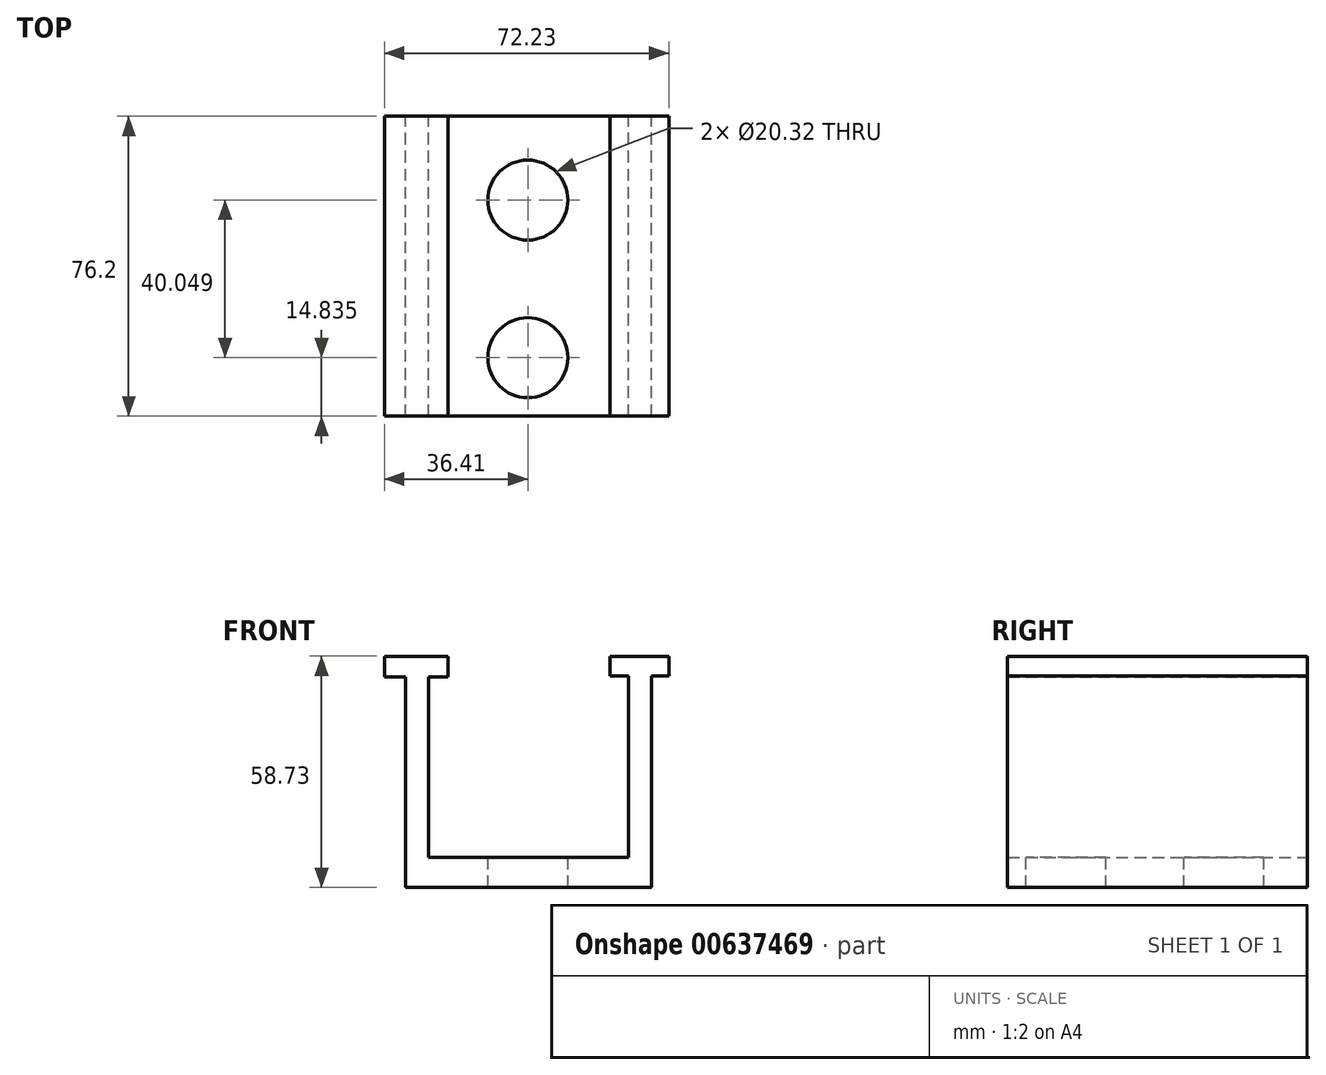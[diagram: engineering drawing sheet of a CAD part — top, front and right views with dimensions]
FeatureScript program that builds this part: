
annotation { "Feature Type Name" : "Feature", "Feature Type Description" : "" }
export const myFeature = defineFeature(function(context is Context, id is Id, definition is map)
    precondition{}
    {
        {
            var Q0;
            Q0=qCreatedBy(makeId("Front.planeOp"),FACE);
            var sketch = newSketch(context, id + "F0", { "sketchPlane" : qUnion([Q0])});
            skLineSegment(sketch, "E0.bottom", {"start": v(-53.88, 30.54) * mm, "end": v(-37.73, 30.54) * mm});
            skLineSegment(sketch, "E0.top", {"start": v(-53.88, 25.25) * mm, "end": v(-37.73, 25.25) * mm});
            skLineSegment(sketch, "E0.left", {"start": v(-53.88, 30.54) * mm, "end": v(-53.88, 25.25) * mm});
            skLineSegment(sketch, "E0.right", {"start": v(-37.73, 30.54) * mm, "end": v(-37.73, 25.25) * mm});
            skLineSegment(sketch, "E1.bottom", {"start": v(3.38, 30.54) * mm, "end": v(18.35, 30.54) * mm});
            skLineSegment(sketch, "E1.top", {"start": v(3.38, 25.54) * mm, "end": v(18.35, 25.54) * mm});
            skLineSegment(sketch, "E1.left", {"start": v(3.38, 30.54) * mm, "end": v(3.38, 25.54) * mm});
            skLineSegment(sketch, "E1.right", {"start": v(18.35, 30.54) * mm, "end": v(18.35, 25.54) * mm});
            skLineSegment(sketch, "E2.bottom", {"start": v(-48.6, 25.25) * mm, "end": v(-42.72, 25.25) * mm});
            skLineSegment(sketch, "E2.top", {"start": v(-48.6, -20.55) * mm, "end": v(-42.72, -20.55) * mm});
            skLineSegment(sketch, "E2.left", {"start": v(-48.6, 25.25) * mm, "end": v(-48.6, -20.55) * mm});
            skLineSegment(sketch, "E2.right", {"start": v(-42.72, 25.25) * mm, "end": v(-42.72, -20.55) * mm});
            skLineSegment(sketch, "E3.bottom", {"start": v(8.07, 25.54) * mm, "end": v(13.95, 25.54) * mm});
            skLineSegment(sketch, "E3.top", {"start": v(8.07, -20.55) * mm, "end": v(13.95, -20.55) * mm});
            skLineSegment(sketch, "E3.left", {"start": v(8.07, 25.54) * mm, "end": v(8.07, -20.55) * mm});
            skLineSegment(sketch, "E3.right", {"start": v(13.95, 25.54) * mm, "end": v(13.95, -20.55) * mm});
            skLineSegment(sketch, "E4.bottom", {"start": v(-48.6, -20.55) * mm, "end": v(13.95, -20.55) * mm});
            skLineSegment(sketch, "E4.top", {"start": v(-48.6, -28.19) * mm, "end": v(13.95, -28.19) * mm});
            skLineSegment(sketch, "E4.left", {"start": v(-48.6, -20.55) * mm, "end": v(-48.6, -28.19) * mm});
            skLineSegment(sketch, "E4.right", {"start": v(13.95, -20.55) * mm, "end": v(13.95, -28.19) * mm});
            skSolve(sketch);
        }
        {
            var Q0;
            Q0 = qSketchRegion(id + "F0", true);
            extrude(context, id + "F1", {"entities" : qUnion([Q0]), "depth" : 76.2 * mm, "offsetDistance" : 25.4 * mm});
        }
        {
            var Q0;
            Q0=makeQuery(id+"F1.opExtrude","SWEPT_FACE",FACE,{"disambiguationData":[OSD([sQuery(id+"F0.wireOp",EDGE,"E4.bottom")])]});
            var sketch = newSketch(context, id + "F2", { "sketchPlane" : qUnion([Q0])});
            skLineSegment(sketch, "E5.left", {"start": v(-26.28, -17.91) * mm, "end": v(-26.28, -61.37) * mm});
            skLineSegment(sketch, "E5.right", {"start": v(-8.66, -17.91) * mm, "end": v(-8.66, -61.37) * mm});
            skArc(sketch, "E6", {"start": v(-8.66, -17.91) * mm, "mid": v(-17.47, -11.87) * mm, "end": v(-26.28, -17.91) * mm});
            skArc(sketch, "E7", {"start": v(-26.28, -61.37) * mm, "mid": v(-17.47, -70.17) * mm, "end": v(-8.66, -61.37) * mm});
            skSolve(sketch);
        }
        {
            var Q0;
            Q0=sQuery(id+"F2.wireOp",VERTEX,"E6.center");
            var Q1;
            Q1=sQuery(id+"F2.wireOp",VERTEX,"E7.center");
            var Q2;
            Q2=makeQuery(id+"F1.opExtrude","SWEPT_BODY",BODY,{"disambiguationData":[OSD([sQuery(id+"F0.wireOp",EDGE,"E0.bottom"),sQuery(id+"F0.wireOp",EDGE,"E0.top"),sQuery(id+"F0.wireOp",EDGE,"E0.left"),sQuery(id+"F0.wireOp",EDGE,"E0.right"),sQuery(id+"F0.wireOp",EDGE,"E1.bottom"),sQuery(id+"F0.wireOp",EDGE,"E1.top"),sQuery(id+"F0.wireOp",EDGE,"E1.left"),sQuery(id+"F0.wireOp",EDGE,"E1.right"),sQuery(id+"F0.wireOp",EDGE,"E2.left"),sQuery(id+"F0.wireOp",EDGE,"E2.right"),sQuery(id+"F0.wireOp",EDGE,"E3.left"),sQuery(id+"F0.wireOp",EDGE,"E3.right"),sQuery(id+"F0.wireOp",EDGE,"E4.bottom"),sQuery(id+"F0.wireOp",EDGE,"E4.top"),sQuery(id+"F0.wireOp",EDGE,"E4.left"),sQuery(id+"F0.wireOp",EDGE,"E4.right")])]});
            hole(context, id + "F3", {"style" : HoleStyle.SIMPLE, "endStyle" : HoleEndStyle.THROUGH, "holeDiameter" : 20.32 * mm, "majorDiameter" : 6.35 * mm, "isTappedThrough" : true, "tappedDepth" : 12.7 * mm, "tapClearance" : 3, "locations" : qUnion([Q0, Q1]), "scope" : qUnion([Q2])});
        }
    });
